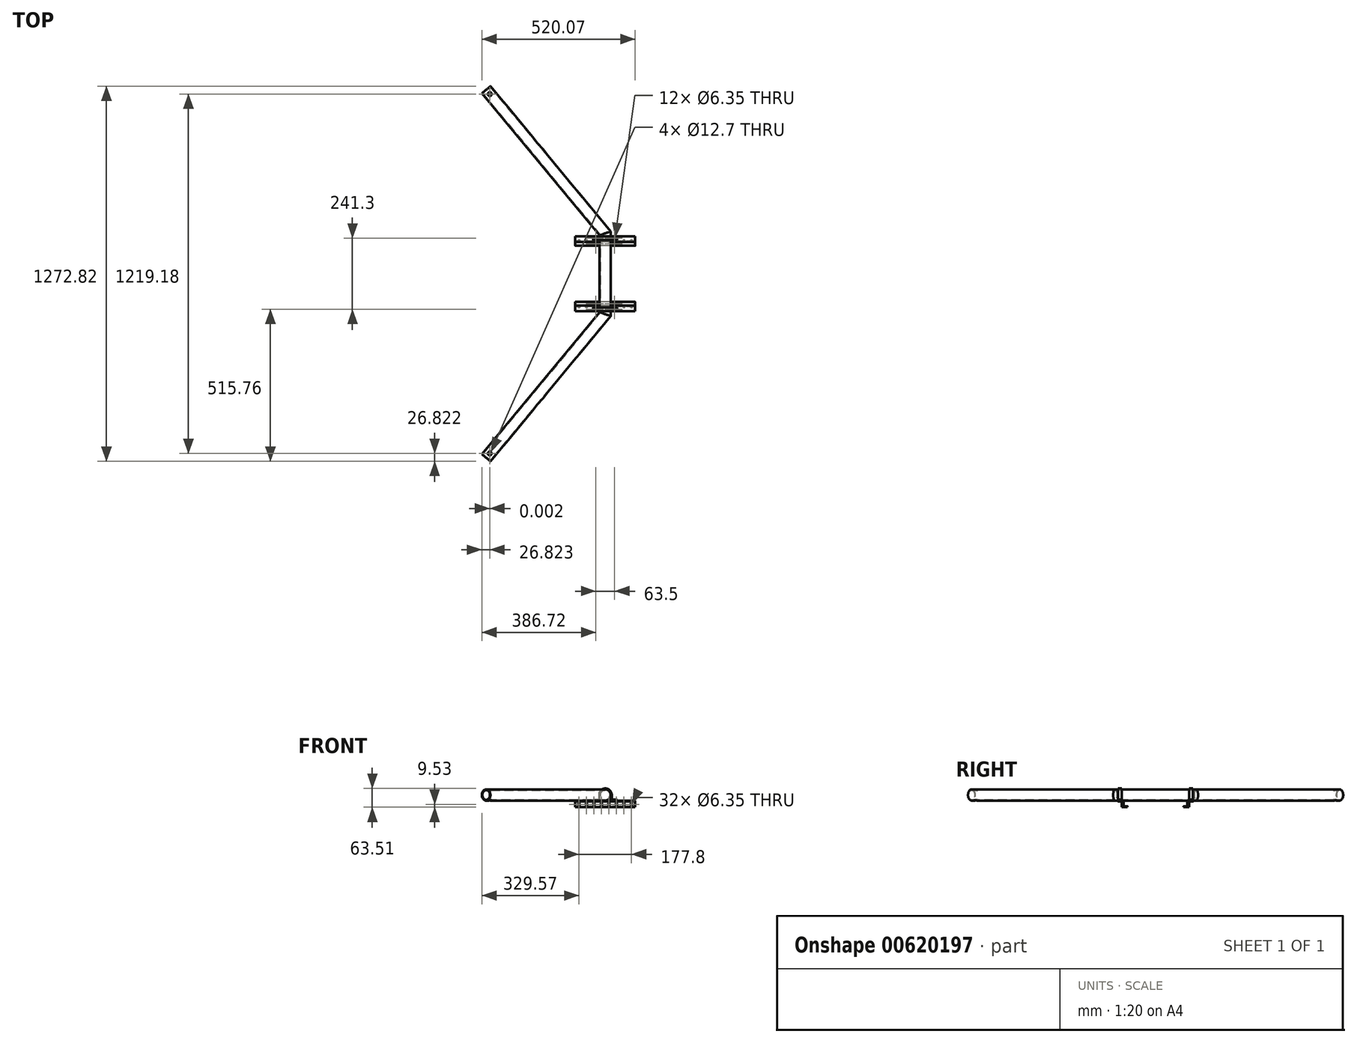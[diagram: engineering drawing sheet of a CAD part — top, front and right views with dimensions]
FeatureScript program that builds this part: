
annotation { "Feature Type Name" : "Feature", "Feature Type Description" : "" }
export const myFeature = defineFeature(function(context is Context, id is Id, definition is map)
    precondition{}
    {
        {
            var Q0;
            Q0=qCreatedBy(makeId("Top.planeOp"),FACE);
            var sketch = newSketch(context, id + "F0", { "sketchPlane" : qUnion([Q0])});
            skLineSegment(sketch, "E0", {"start": v(-403.8, 624.26) * mm, "end": v(0, 137.16) * mm});
            skLineSegment(sketch, "E1", {"start": v(0, -137.16) * mm, "end": v(-403.8, -624.25) * mm});
            skLineSegment(sketch, "E2", {"start": v(0, 137.16) * mm, "end": v(0, -137.16) * mm, "construction": true});
            skLineSegment(sketch, "E3", {"start": v(0, 137.16) * mm, "end": v(0, -137.16) * mm});
            skSolve(sketch);
        }
        {
            var Q0;
            Q0=qCreatedBy(makeId("Front.planeOp"),FACE);
            var sketch = newSketch(context, id + "F1", { "sketchPlane" : qUnion([Q0])});
            skCircle(sketch, "E4", {"center": v(0, 0) * mm, "radius": 19.05 * mm});
            skSolve(sketch);
        }
        {
            var Q0;
            Q0 = qSketchRegion(id + "F1", true);
            var Q1;
            Q1=sQuery(id+"F0.wireOp",EDGE,"E3");
            var Q2;
            Q2=sQuery(id+"F0.wireOp",EDGE,"E1");
            var Q3;
            Q3=sQuery(id+"F0.wireOp",EDGE,"E0");
            sweep(context, id + "F2", {"profiles" : qUnion([Q0]), "path" : qUnion([Q1, Q2, Q3])});
        }
        {
            var Q0;
            Q0=makeQuery(id+"F2.opSweep","CAP_FACE",FACE,{"disambiguationData":[OSD([sQuery(id+"F0.wireOp",VERTEX,"E1.end"),sQuery(id+"F1.wireOp",EDGE,"E4")])],"isStart":false});
            var Q1;
            Q1=makeQuery(id+"F2.opSweep","CAP_FACE",FACE,{"disambiguationData":[OSD([sQuery(id+"F0.wireOp",VERTEX,"E0.start"),sQuery(id+"F1.wireOp",EDGE,"E4")])],"isStart":true});
            var Q2;
            Q2=makeQuery(id+"FkxEvqe9UlPCQNw_2.opSweep","CAP_FACE",FACE,{"disambiguationData":[OSD([sQuery(id+"F0.wireOp",VERTEX,"E0.start"),sQuery(id+"F1.wireOp",EDGE,"E4")])],"isStart":false});
            shell(context, id + "F3", {"entities" : qUnion([Q0, Q1, Q2]), "thickness" : 2.54 * mm});
        }
        {
            var Q0;
            Q0=qCreatedBy(makeId("Top.planeOp"),FACE);
            var sketch = newSketch(context, id + "F4", { "sketchPlane" : qUnion([Q0])});
            skCircle(sketch, "E5", {"center": v(-391.65, -609.59) * mm, "radius": 6.35 * mm});
            skCircle(sketch, "E6", {"center": v(-391.64, 609.59) * mm, "radius": 6.35 * mm});
            skSolve(sketch);
        }
        {
            var Q0;
            Q0 = qSketchRegion(id + "F4", true);
            extrude(context, id + "F5", {"entities" : qUnion([Q0]), "operationType" : NewBodyOperationType.REMOVE, "depth" : 116.84 * mm, "offsetDistance" : 25.4 * mm, "hasSecondDirection" : true, "secondDirectionOppositeDirection" : true, "secondDirectionDepth" : 25.4 * mm});
        }
        {
            var Q0;
            Q0=qCreatedBy(makeId("Right.planeOp"),FACE);
            var sketch = newSketch(context, id + "F6", { "sketchPlane" : qUnion([Q0])});
            skLineSegment(sketch, "E7.bottom", {"start": v(-110.57, -38.1) * mm, "end": v(-95.8, -38.1) * mm});
            skLineSegment(sketch, "E7.top", {"start": v(-111.12, -41.28) * mm, "end": v(-95.25, -41.28) * mm});
            skLineSegment(sketch, "E7.right", {"start": v(-95.25, -38.65) * mm, "end": v(-95.25, -41.28) * mm});
            skLineSegment(sketch, "E8.bottom", {"start": v(-111.12, -41.27) * mm, "end": v(-114.3, -41.27) * mm});
            skLineSegment(sketch, "E8.top", {"start": v(-111.68, -22.23) * mm, "end": v(-113.75, -22.23) * mm});
            skLineSegment(sketch, "E8.left", {"start": v(-111.12, -37.55) * mm, "end": v(-111.12, -22.78) * mm});
            skLineSegment(sketch, "E8.right", {"start": v(-114.3, -41.28) * mm, "end": v(-114.3, -22.78) * mm});
            skPoint(sketch, "E9.visualSharp", {"position": v(-114.3, -22.23) * mm});
            skArc(sketch, "E9.filletArc", {"start": v(-113.75, -22.22) * mm, "mid": v(-114.14, -22.39) * mm, "end": v(-114.3, -22.78) * mm});
            skPoint(sketch, "E10.visualSharp", {"position": v(-111.12, -22.23) * mm});
            skArc(sketch, "E10.filletArc", {"start": v(-111.12, -22.78) * mm, "mid": v(-111.29, -22.39) * mm, "end": v(-111.68, -22.23) * mm});
            skPoint(sketch, "E11.visualSharp", {"position": v(-111.12, -38.1) * mm});
            skArc(sketch, "E11.filletArc", {"start": v(-111.12, -37.55) * mm, "mid": v(-110.96, -37.94) * mm, "end": v(-110.57, -38.1) * mm});
            skPoint(sketch, "E12.visualSharp", {"position": v(-95.25, -38.1) * mm});
            skArc(sketch, "E12.filletArc", {"start": v(-95.25, -38.65) * mm, "mid": v(-95.41, -38.26) * mm, "end": v(-95.8, -38.1) * mm});
            skLineSegment(sketch, "E13.MirrorCS", {"start": v(111.68, -22.23) * mm, "end": v(113.75, -22.23) * mm});
            skArc(sketch, "E14.MirrorCS", {"start": v(111.12, -22.78) * mm, "mid": v(111.29, -22.39) * mm, "end": v(111.68, -22.23) * mm});
            skArc(sketch, "E15.MirrorCS", {"start": v(113.75, -22.22) * mm, "mid": v(114.14, -22.39) * mm, "end": v(114.3, -22.78) * mm});
            skLineSegment(sketch, "E16.MirrorCS", {"start": v(95.25, -38.65) * mm, "end": v(95.25, -41.28) * mm});
            skArc(sketch, "E17.MirrorCS", {"start": v(95.25, -38.65) * mm, "mid": v(95.41, -38.26) * mm, "end": v(95.8, -38.1) * mm});
            skArc(sketch, "E18.MirrorCS", {"start": v(111.12, -37.55) * mm, "mid": v(110.96, -37.94) * mm, "end": v(110.57, -38.1) * mm});
            skLineSegment(sketch, "E19.MirrorCS", {"start": v(111.12, -41.27) * mm, "end": v(114.3, -41.27) * mm});
            skLineSegment(sketch, "E20.MirrorCS", {"start": v(110.57, -38.1) * mm, "end": v(95.8, -38.1) * mm});
            skPoint(sketch, "E21.MirrorP", {"position": v(95.25, -38.1) * mm});
            skPoint(sketch, "E22.MirrorP", {"position": v(111.12, -22.23) * mm});
            skLineSegment(sketch, "E23.MirrorCS", {"start": v(111.12, -37.55) * mm, "end": v(111.12, -22.78) * mm});
            skLineSegment(sketch, "E24.MirrorCS", {"start": v(111.12, -41.27) * mm, "end": v(95.25, -41.27) * mm});
            skPoint(sketch, "E25.MirrorP", {"position": v(114.3, -22.23) * mm});
            skLineSegment(sketch, "E26.MirrorCS", {"start": v(114.3, -41.28) * mm, "end": v(114.3, -22.78) * mm});
            skPoint(sketch, "E27.MirrorP", {"position": v(111.12, -38.1) * mm});
            skSolve(sketch);
        }
        {
            var Q0;
            Q0 = qSketchRegion(id + "F6", true);
            extrude(context, id + "F7", {"entities" : qUnion([Q0]), "depth" : 101.6 * mm, "offsetDistance" : 25.4 * mm, "hasSecondDirection" : true, "secondDirectionOppositeDirection" : true, "secondDirectionDepth" : 101.6 * mm});
        }
        {
            var Q0;
            Q0=qCreatedBy(makeId("Right.planeOp"),FACE);
            var sketch = newSketch(context, id + "F8", { "sketchPlane" : qUnion([Q0])});
            skLineSegment(sketch, "E28.bottom", {"start": v(-127, -19.05) * mm, "end": v(-107.95, -19.05) * mm});
            skLineSegment(sketch, "E28.top", {"start": v(-126.45, -22.23) * mm, "end": v(-111.68, -22.23) * mm});
            skLineSegment(sketch, "E28.left", {"start": v(-127, -19.05) * mm, "end": v(-127, -21.67) * mm});
            skLineSegment(sketch, "E28.right", {"start": v(-107.95, -19.05) * mm, "end": v(-107.95, -22.23) * mm});
            skLineSegment(sketch, "E29.top", {"start": v(-108.5, -38.1) * mm, "end": v(-110.57, -38.1) * mm});
            skLineSegment(sketch, "E29.left", {"start": v(-107.95, -22.23) * mm, "end": v(-107.95, -37.55) * mm});
            skLineSegment(sketch, "E29.right", {"start": v(-111.12, -22.78) * mm, "end": v(-111.12, -37.55) * mm});
            skPoint(sketch, "E30.visualSharp", {"position": v(-111.12, -22.23) * mm});
            skArc(sketch, "E30.filletArc", {"start": v(-111.12, -22.78) * mm, "mid": v(-111.29, -22.39) * mm, "end": v(-111.68, -22.22) * mm});
            skPoint(sketch, "E31.visualSharp", {"position": v(-127, -22.23) * mm});
            skArc(sketch, "E31.filletArc", {"start": v(-127, -21.67) * mm, "mid": v(-126.84, -22.06) * mm, "end": v(-126.45, -22.22) * mm});
            skPoint(sketch, "E32.visualSharp", {"position": v(-111.13, -38.1) * mm});
            skArc(sketch, "E32.filletArc", {"start": v(-111.13, -37.55) * mm, "mid": v(-110.96, -37.94) * mm, "end": v(-110.57, -38.1) * mm});
            skPoint(sketch, "E33.visualSharp", {"position": v(-107.95, -38.1) * mm});
            skArc(sketch, "E33.filletArc", {"start": v(-108.5, -38.1) * mm, "mid": v(-108.11, -37.94) * mm, "end": v(-107.95, -37.55) * mm});
            skArc(sketch, "E34.MirrorCS", {"start": v(111.13, -37.55) * mm, "mid": v(110.96, -37.94) * mm, "end": v(110.57, -38.1) * mm});
            skArc(sketch, "E35.MirrorCS", {"start": v(108.5, -38.1) * mm, "mid": v(108.11, -37.94) * mm, "end": v(107.95, -37.55) * mm});
            skLineSegment(sketch, "E36.MirrorCS", {"start": v(108.5, -38.1) * mm, "end": v(110.57, -38.1) * mm});
            skArc(sketch, "E37.MirrorCS", {"start": v(127, -21.67) * mm, "mid": v(126.84, -22.06) * mm, "end": v(126.45, -22.22) * mm});
            skArc(sketch, "E38.MirrorCS", {"start": v(111.12, -22.78) * mm, "mid": v(111.29, -22.39) * mm, "end": v(111.68, -22.22) * mm});
            skLineSegment(sketch, "E39.MirrorCS", {"start": v(107.95, -19.05) * mm, "end": v(107.95, -22.23) * mm});
            skLineSegment(sketch, "E40.MirrorCS", {"start": v(127, -19.05) * mm, "end": v(127, -21.67) * mm});
            skPoint(sketch, "E41.MirrorP", {"position": v(127, -22.23) * mm});
            skLineSegment(sketch, "E42.MirrorCS", {"start": v(126.45, -22.23) * mm, "end": v(111.68, -22.23) * mm});
            skLineSegment(sketch, "E43.MirrorCS", {"start": v(111.12, -22.78) * mm, "end": v(111.12, -37.55) * mm});
            skLineSegment(sketch, "E44.MirrorCS", {"start": v(107.95, -22.23) * mm, "end": v(107.95, -37.55) * mm});
            skPoint(sketch, "E45.MirrorP", {"position": v(111.13, -38.1) * mm});
            skPoint(sketch, "E46.MirrorP", {"position": v(111.12, -22.23) * mm});
            skPoint(sketch, "E47.MirrorP", {"position": v(107.95, -38.1) * mm});
            skLineSegment(sketch, "E48.MirrorCS", {"start": v(127, -19.05) * mm, "end": v(107.95, -19.05) * mm});
            skSolve(sketch);
        }
        {
            var Q0;
            Q0 = qSketchRegion(id + "F8", true);
            extrude(context, id + "F9", {"entities" : qUnion([Q0]), "depth" : 101.6 * mm, "offsetDistance" : 25.4 * mm, "hasSecondDirection" : true, "secondDirectionOppositeDirection" : true, "secondDirectionDepth" : 101.6 * mm});
        }
        {
            var Q0;
            Q0=makeQuery(id+"F9.opExtrude","SWEPT_FACE",FACE,{"disambiguationData":[OSD([sQuery(id+"F8.wireOp",EDGE,"E28.right"),sQuery(id+"F8.wireOp",EDGE,"E29.left")])]});
            var sketch = newSketch(context, id + "F10", { "sketchPlane" : qUnion([Q0])});
            skLineSegment(sketch, "E49.bottom", {"start": v(-19.05, 0) * mm, "end": v(-22.23, 0) * mm});
            skLineSegment(sketch, "E49.top", {"start": v(-19.05, -19.05) * mm, "end": v(-22.23, -19.05) * mm});
            skLineSegment(sketch, "E49.left", {"start": v(-19.05, 0) * mm, "end": v(-19.05, -19.05) * mm});
            skLineSegment(sketch, "E49.right", {"start": v(-22.23, 0) * mm, "end": v(-22.23, -15.32) * mm});
            skLineSegment(sketch, "E50.bottom", {"start": v(-22.23, -19.05) * mm, "end": v(-40.48, -19.05) * mm});
            skLineSegment(sketch, "E50.top", {"start": v(-22.78, -15.87) * mm, "end": v(-39.93, -15.87) * mm});
            skLineSegment(sketch, "E50.right", {"start": v(-40.48, -19.05) * mm, "end": v(-40.48, -16.43) * mm});
            skArc(sketch, "E51", {"start": v(19.05, 0) * mm, "mid": v(0, 19.05) * mm, "end": v(-19.05, 0) * mm});
            skArc(sketch, "E52", {"start": v(22.22, 0) * mm, "mid": v(0, 22.23) * mm, "end": v(-22.23, 0) * mm});
            skLineSegment(sketch, "E53.MirrorCS", {"start": v(40.48, -19.05) * mm, "end": v(40.48, -16.43) * mm});
            skLineSegment(sketch, "E54.MirrorCS", {"start": v(19.05, 0) * mm, "end": v(22.23, 0) * mm});
            skLineSegment(sketch, "E55.MirrorCS", {"start": v(19.05, -19.05) * mm, "end": v(22.23, -19.05) * mm});
            skLineSegment(sketch, "E56.MirrorCS", {"start": v(22.78, -15.87) * mm, "end": v(39.93, -15.87) * mm});
            skLineSegment(sketch, "E57.MirrorCS", {"start": v(22.23, -19.05) * mm, "end": v(40.48, -19.05) * mm});
            skLineSegment(sketch, "E58.MirrorCS", {"start": v(22.23, 0) * mm, "end": v(22.23, -15.32) * mm});
            skLineSegment(sketch, "E59.MirrorCS", {"start": v(19.05, 0) * mm, "end": v(19.05, -19.05) * mm});
            skPoint(sketch, "E60.visualSharp", {"position": v(-40.48, -15.87) * mm});
            skArc(sketch, "E60.filletArc", {"start": v(-39.93, -15.87) * mm, "mid": v(-40.32, -16.04) * mm, "end": v(-40.48, -16.43) * mm});
            skPoint(sketch, "E61.visualSharp", {"position": v(-22.23, -15.87) * mm});
            skArc(sketch, "E61.filletArc", {"start": v(-22.78, -15.87) * mm, "mid": v(-22.39, -15.71) * mm, "end": v(-22.23, -15.32) * mm});
            skPoint(sketch, "E62.visualSharp", {"position": v(22.23, -15.87) * mm});
            skArc(sketch, "E62.filletArc", {"start": v(22.23, -15.32) * mm, "mid": v(22.39, -15.71) * mm, "end": v(22.78, -15.87) * mm});
            skPoint(sketch, "E63.visualSharp", {"position": v(40.48, -15.87) * mm});
            skArc(sketch, "E63.filletArc", {"start": v(40.48, -16.43) * mm, "mid": v(40.32, -16.04) * mm, "end": v(39.93, -15.87) * mm});
            skSolve(sketch);
        }
        {
            var Q0;
            Q0 = qSketchRegion(id + "F10", true);
            var Q1;
            Q1=makeQuery(id+"F9.opExtrude","SWEPT_FACE",FACE,{"disambiguationData":[OSD([sQuery(id+"F8.wireOp",EDGE,"E28.left")])]});
            extrude(context, id + "F11", {"entities" : qUnion([Q0]), "oppositeDirection" : true, "depth" : 12.7 * mm, "endBoundEntityFace" : qUnion([Q1]), "offsetDistance" : 25.4 * mm});
        }
        {
            var Q0;
            Q0=makeQuery(id+"F9.opExtrude","SWEPT_FACE",FACE,{"disambiguationData":[OSD([sQuery(id+"F8.wireOp",EDGE,"E39.MirrorCS"),sQuery(id+"F8.wireOp",EDGE,"E44.MirrorCS")])]});
            var sketch = newSketch(context, id + "F12", { "sketchPlane" : qUnion([Q0])});
            skLineSegment(sketch, "E64.top", {"start": v(-19.05, -19.05) * mm, "end": v(-22.22, -19.05) * mm});
            skLineSegment(sketch, "E64.left", {"start": v(-19.05, 0) * mm, "end": v(-19.05, -19.05) * mm});
            skLineSegment(sketch, "E64.right", {"start": v(-22.22, 0) * mm, "end": v(-22.22, -15.32) * mm});
            skLineSegment(sketch, "E65.bottom", {"start": v(-22.22, -19.05) * mm, "end": v(-40.48, -19.05) * mm});
            skLineSegment(sketch, "E65.top", {"start": v(-22.78, -15.88) * mm, "end": v(-39.93, -15.88) * mm});
            skLineSegment(sketch, "E65.right", {"start": v(-40.48, -19.05) * mm, "end": v(-40.48, -16.43) * mm});
            skArc(sketch, "E66", {"start": v(19.05, 0) * mm, "mid": v(0, 19.05) * mm, "end": v(-19.05, 0) * mm});
            skArc(sketch, "E67", {"start": v(22.23, 0) * mm, "mid": v(0, 22.22) * mm, "end": v(-22.22, 0) * mm});
            skLineSegment(sketch, "E68.MirrorCS", {"start": v(40.48, -19.05) * mm, "end": v(40.48, -16.43) * mm});
            skLineSegment(sketch, "E69.MirrorCS", {"start": v(19.05, -19.05) * mm, "end": v(22.23, -19.05) * mm});
            skLineSegment(sketch, "E70.MirrorCS", {"start": v(22.78, -15.88) * mm, "end": v(39.93, -15.88) * mm});
            skLineSegment(sketch, "E71.MirrorCS", {"start": v(22.23, -19.05) * mm, "end": v(40.48, -19.05) * mm});
            skLineSegment(sketch, "E72.MirrorCS", {"start": v(22.23, 0) * mm, "end": v(22.23, -15.32) * mm});
            skLineSegment(sketch, "E73.MirrorCS", {"start": v(19.05, 0) * mm, "end": v(19.05, -19.05) * mm});
            skPoint(sketch, "E74.visualSharp", {"position": v(-40.48, -15.88) * mm});
            skArc(sketch, "E74.filletArc", {"start": v(-39.93, -15.88) * mm, "mid": v(-40.32, -16.04) * mm, "end": v(-40.48, -16.43) * mm});
            skPoint(sketch, "E75.visualSharp", {"position": v(-22.22, -15.88) * mm});
            skArc(sketch, "E75.filletArc", {"start": v(-22.78, -15.88) * mm, "mid": v(-22.39, -15.71) * mm, "end": v(-22.22, -15.32) * mm});
            skPoint(sketch, "E76.visualSharp", {"position": v(22.23, -15.88) * mm});
            skArc(sketch, "E76.filletArc", {"start": v(22.23, -15.32) * mm, "mid": v(22.39, -15.71) * mm, "end": v(22.78, -15.88) * mm});
            skPoint(sketch, "E77.visualSharp", {"position": v(40.48, -15.88) * mm});
            skArc(sketch, "E77.filletArc", {"start": v(40.48, -16.43) * mm, "mid": v(40.32, -16.04) * mm, "end": v(39.93, -15.88) * mm});
            skSolve(sketch);
        }
        {
            var Q0;
            Q0 = qSketchRegion(id + "F12", true);
            var Q1;
            Q1=makeQuery(id+"F9.opExtrude","SWEPT_FACE",FACE,{"disambiguationData":[OSD([sQuery(id+"F8.wireOp",EDGE,"E40.MirrorCS")])]});
            extrude(context, id + "F13", {"entities" : qUnion([Q0]), "oppositeDirection" : true, "depth" : 12.7 * mm, "endBoundEntityFace" : qUnion([Q1]), "offsetDistance" : 25.4 * mm});
        }
        {
            var Q0;
            Q0=makeQuery(id+"F11.opExtrude","SWEPT_BODY",BODY,{"disambiguationData":[OSD([sQuery(id+"F10.wireOp",EDGE,"E49.top"),sQuery(id+"F10.wireOp",EDGE,"E49.left"),sQuery(id+"F10.wireOp",EDGE,"E49.right"),sQuery(id+"F10.wireOp",EDGE,"E50.bottom"),sQuery(id+"F10.wireOp",EDGE,"E50.top"),sQuery(id+"F10.wireOp",EDGE,"E50.right"),sQuery(id+"F10.wireOp",EDGE,"E51"),sQuery(id+"F10.wireOp",EDGE,"E52"),sQuery(id+"F10.wireOp",EDGE,"E53.MirrorCS"),sQuery(id+"F10.wireOp",EDGE,"E55.MirrorCS"),sQuery(id+"F10.wireOp",EDGE,"E56.MirrorCS"),sQuery(id+"F10.wireOp",EDGE,"E57.MirrorCS"),sQuery(id+"F10.wireOp",EDGE,"E58.MirrorCS"),sQuery(id+"F10.wireOp",EDGE,"E59.MirrorCS"),sQuery(id+"F10.wireOp",EDGE,"E60.filletArc"),sQuery(id+"F10.wireOp",EDGE,"E61.filletArc"),sQuery(id+"F10.wireOp",EDGE,"E62.filletArc"),sQuery(id+"F10.wireOp",EDGE,"E63.filletArc")])]});
            transform(context, id + "F14", {"entities" : qUnion([Q0]), "transformType" : TransformType.TRANSLATION_3D, "dx" : 0 * mm, "dy" : -6.35 * mm, "dz" : 0 * mm, "makeCopy" : false});
        }
        {
            var Q0;
            Q0=makeQuery(id+"F13.opExtrude","SWEPT_BODY",BODY,{"disambiguationData":[OSD([sQuery(id+"F12.wireOp",EDGE,"E64.top"),sQuery(id+"F12.wireOp",EDGE,"E64.left"),sQuery(id+"F12.wireOp",EDGE,"E64.right"),sQuery(id+"F12.wireOp",EDGE,"E65.bottom"),sQuery(id+"F12.wireOp",EDGE,"E65.top"),sQuery(id+"F12.wireOp",EDGE,"E65.right"),sQuery(id+"F12.wireOp",EDGE,"E66"),sQuery(id+"F12.wireOp",EDGE,"E67"),sQuery(id+"F12.wireOp",EDGE,"E68.MirrorCS"),sQuery(id+"F12.wireOp",EDGE,"E69.MirrorCS"),sQuery(id+"F12.wireOp",EDGE,"E70.MirrorCS"),sQuery(id+"F12.wireOp",EDGE,"E71.MirrorCS"),sQuery(id+"F12.wireOp",EDGE,"E72.MirrorCS"),sQuery(id+"F12.wireOp",EDGE,"E73.MirrorCS"),sQuery(id+"F12.wireOp",EDGE,"E74.filletArc"),sQuery(id+"F12.wireOp",EDGE,"E75.filletArc"),sQuery(id+"F12.wireOp",EDGE,"E76.filletArc"),sQuery(id+"F12.wireOp",EDGE,"E77.filletArc")])]});
            transform(context, id + "F15", {"entities" : qUnion([Q0]), "transformType" : TransformType.TRANSLATION_3D, "dx" : 0 * mm, "dy" : 6.35 * mm, "dz" : 0 * mm, "makeCopy" : false});
        }
        {
            var Q0;
            Q0=qCreatedBy(makeId("Top.planeOp"),FACE);
            var sketch = newSketch(context, id + "F16", { "sketchPlane" : qUnion([Q0])});
            skCircle(sketch, "E78", {"center": v(-31.75, -120.65) * mm, "radius": 3.18 * mm});
            skCircle(sketch, "E79.MirrorC", {"center": v(31.75, -120.65) * mm, "radius": 3.18 * mm});
            skCircle(sketch, "E80.MirrorC", {"center": v(-31.75, 120.65) * mm, "radius": 3.18 * mm});
            skCircle(sketch, "E81.MirrorC", {"center": v(31.75, 120.65) * mm, "radius": 3.18 * mm});
            skSolve(sketch);
        }
        {
            var Q0;
            Q0 = qSketchRegion(id + "F16", true);
            extrude(context, id + "F17", {"entities" : qUnion([Q0]), "operationType" : NewBodyOperationType.REMOVE, "oppositeDirection" : true, "depth" : 25.4 * mm, "offsetDistance" : 25.4 * mm});
        }
        {
            var Q0;
            Q0=qCreatedBy(makeId("Front.planeOp"),FACE);
            var sketch = newSketch(context, id + "F18", { "sketchPlane" : qUnion([Q0])});
            skCircle(sketch, "E82", {"center": v(88.9, -31.75) * mm, "radius": 3.18 * mm});
            skCircle(sketch, "E83.1.0.0", {"center": v(63.5, -31.75) * mm, "radius": 3.18 * mm});
            skCircle(sketch, "E83.2.0.0", {"center": v(38.1, -31.75) * mm, "radius": 3.18 * mm});
            skCircle(sketch, "E83.3.0.0", {"center": v(12.7, -31.75) * mm, "radius": 3.18 * mm});
            skCircle(sketch, "E83.4.0.0", {"center": v(-12.7, -31.75) * mm, "radius": 3.18 * mm});
            skCircle(sketch, "E83.5.0.0", {"center": v(-38.1, -31.75) * mm, "radius": 3.18 * mm});
            skCircle(sketch, "E83.6.0.0", {"center": v(-63.5, -31.75) * mm, "radius": 3.18 * mm});
            skCircle(sketch, "E83.7.0.0", {"center": v(-88.9, -31.75) * mm, "radius": 3.18 * mm});
            skLineSegment(sketch, "E83.direction1", {"start": v(88.9, -31.75) * mm, "end": v(63.5, -31.75) * mm, "construction": true});
            skSolve(sketch);
        }
        {
            var Q0;
            Q0 = qSketchRegion(id + "F18", true);
            extrude(context, id + "F19", {"entities" : qUnion([Q0]), "operationType" : NewBodyOperationType.REMOVE, "depth" : 128.78 * mm, "offsetDistance" : 25.4 * mm, "hasSecondDirection" : true, "secondDirectionOppositeDirection" : true, "secondDirectionDepth" : 151.9 * mm});
        }
        {
            var Q0;
            Q0=qCreatedBy(makeId("Top.planeOp"),FACE);
            var sketch = newSketch(context, id + "F20", { "sketchPlane" : qUnion([Q0])});
            skCircle(sketch, "E84", {"center": v(-31.75, -101.6) * mm, "radius": 3.18 * mm});
            skCircle(sketch, "E85.MirrorC", {"center": v(31.75, -101.6) * mm, "radius": 3.18 * mm});
            skCircle(sketch, "E86.MirrorC", {"center": v(-31.75, 101.6) * mm, "radius": 3.18 * mm});
            skCircle(sketch, "E87.MirrorC", {"center": v(31.75, 101.6) * mm, "radius": 3.18 * mm});
            skSolve(sketch);
        }
        {
            var Q0;
            Q0 = qSketchRegion(id + "F20", true);
            extrude(context, id + "F21", {"entities" : qUnion([Q0]), "operationType" : NewBodyOperationType.REMOVE, "oppositeDirection" : true, "depth" : 100.08 * mm, "offsetDistance" : 25.4 * mm});
        }
    });
